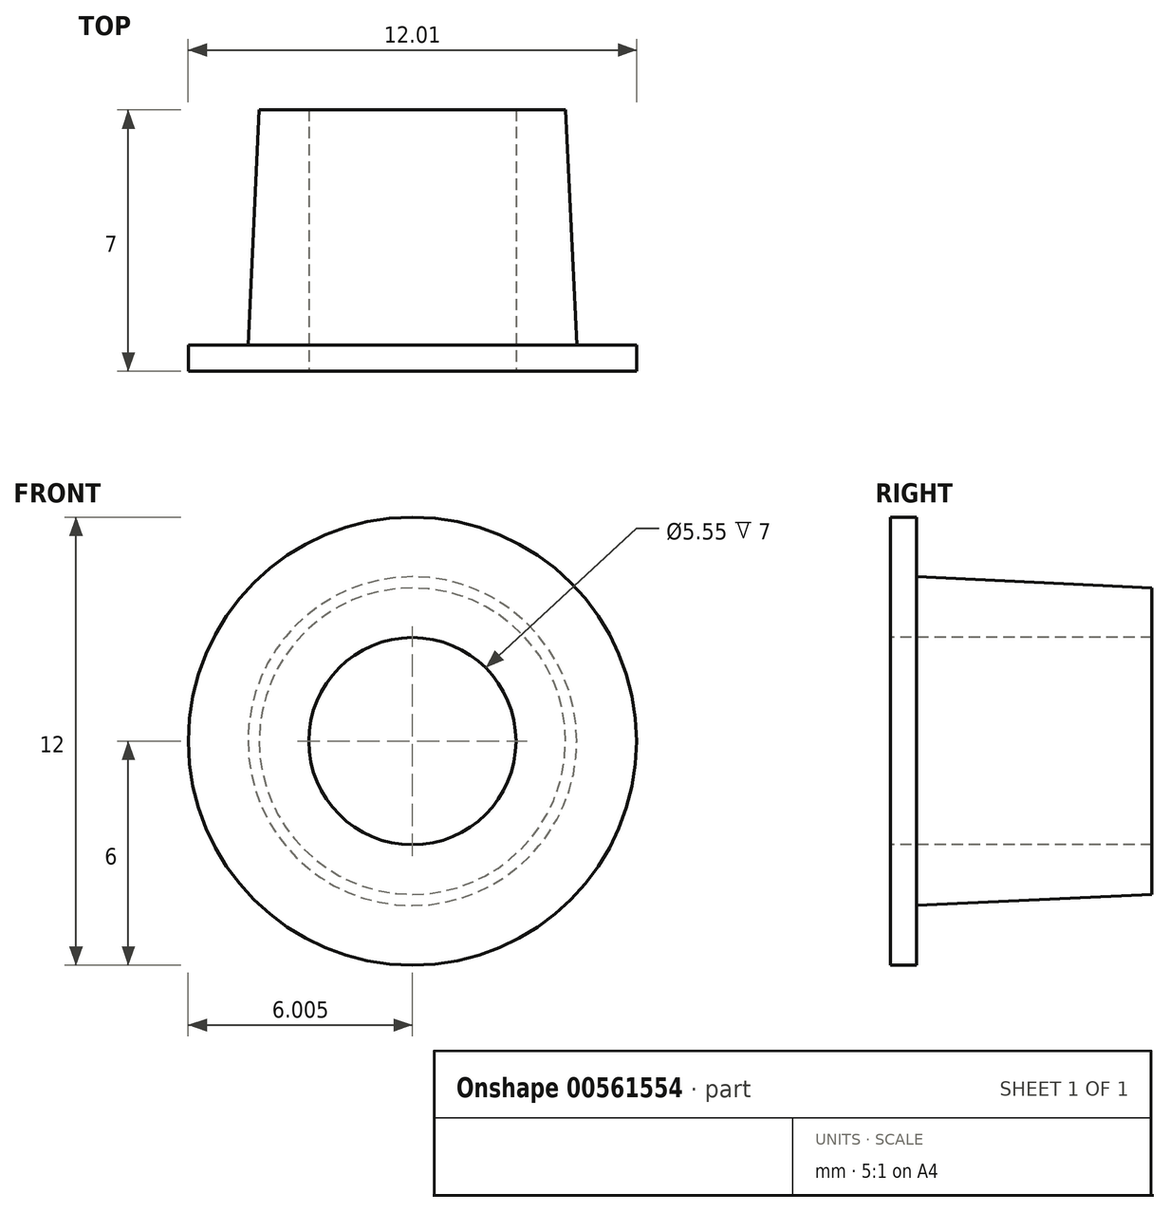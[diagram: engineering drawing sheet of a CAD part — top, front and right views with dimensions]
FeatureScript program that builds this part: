
annotation { "Feature Type Name" : "Feature", "Feature Type Description" : "" }
export const myFeature = defineFeature(function(context is Context, id is Id, definition is map)
    precondition{}
    {
        {
            var Q0;
            Q0=qCreatedBy(makeId("Top.planeOp"),FACE);
            var sketch = newSketch(context, id + "F0", { "sketchPlane" : qUnion([Q0])});
            skLineSegment(sketch, "E0", {"start": v(0, 0) * mm, "end": v(3.23, 0) * mm});
            skLineSegment(sketch, "E1", {"start": v(3.23, 0) * mm, "end": v(3.23, 0.7) * mm});
            skLineSegment(sketch, "E2", {"start": v(3.23, 0.7) * mm, "end": v(1.63, 0.7) * mm});
            skLineSegment(sketch, "E3", {"start": v(1.32, 7) * mm, "end": v(0, 7) * mm});
            skLineSegment(sketch, "E4", {"start": v(0, 7) * mm, "end": v(0, 0) * mm});
            skLineSegment(sketch, "E5", {"start": v(-2.77, 0) * mm, "end": v(-2.77, 2.82) * mm, "construction": true});
            skLineSegment(sketch, "E6", {"start": v(1.32, 7) * mm, "end": v(1.63, 0.7) * mm});
            skSolve(sketch);
        }
        {
            var Q0;
            Q0 = qSketchRegion(id + "F0", true);
            var Q1;
            Q1=sQuery(id+"F0.wireOp",EDGE,"E5");
            revolve(context, id + "F1", {"entities" : qUnion([Q0]), "axis" : qUnion([Q1]), "revolveType" : RevolveType.FULL});
        }
    });
